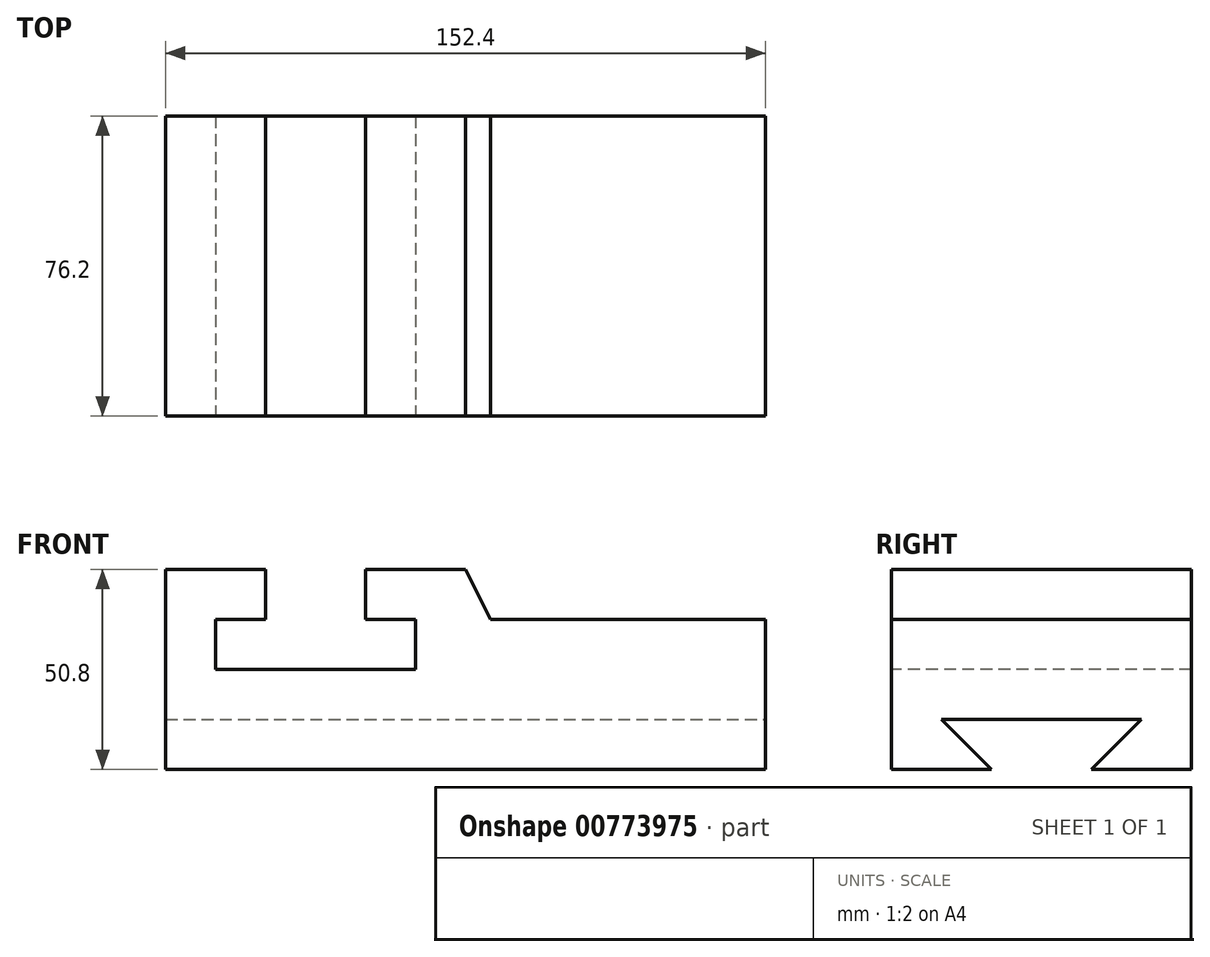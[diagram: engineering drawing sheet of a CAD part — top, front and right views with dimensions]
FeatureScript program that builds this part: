
annotation { "Feature Type Name" : "Feature", "Feature Type Description" : "" }
export const myFeature = defineFeature(function(context is Context, id is Id, definition is map)
    precondition{}
    {
        {
            var Q0;
            Q0=qCreatedBy(makeId("Front.planeOp"),FACE);
            var sketch = newSketch(context, id + "F0", { "sketchPlane" : qUnion([Q0])});
            skLineSegment(sketch, "E0", {"start": v(0, 0) * mm, "end": v(152.4, 0) * mm});
            skLineSegment(sketch, "E1", {"start": v(152.4, 0) * mm, "end": v(152.4, 50.8) * mm});
            skLineSegment(sketch, "E2", {"start": v(152.4, 50.8) * mm, "end": v(0, 50.8) * mm});
            skLineSegment(sketch, "E3", {"start": v(0, 50.8) * mm, "end": v(0, 0) * mm});
            skSolve(sketch);
        }
        {
            var Q0;
            Q0=makeQuery(id+"F0.imprint","IMPRINT",FACE,{"disambiguationData":[TD([[makeQuery(id+"F0.imprint","IMPRINT",EDGE,{"derivedFrom":sQuery(id+"F0.wireOp",EDGE,"E0")}),1.0]])]});
            extrude(context, id + "F1", {"entities" : qUnion([Q0]), "depth" : 76.2 * mm, "offsetDistance" : 25.4 * mm});
        }
        {
            var Q0;
            Q0=makeQuery(id+"F1.opExtrude","CAP_FACE",FACE,{"disambiguationData":[OSD([sQuery(id+"F0.wireOp",EDGE,"E0"),sQuery(id+"F0.wireOp",EDGE,"E1"),sQuery(id+"F0.wireOp",EDGE,"E2"),sQuery(id+"F0.wireOp",EDGE,"E3")])],"isStart":false});
            var sketch = newSketch(context, id + "F2", { "sketchPlane" : qUnion([Q0])});
            skLineSegment(sketch, "E4", {"start": v(152.4, 50.8) * mm, "end": v(152.4, 38.1) * mm});
            skLineSegment(sketch, "E5", {"start": v(152.4, 38.1) * mm, "end": v(82.55, 38.1) * mm});
            skLineSegment(sketch, "E6", {"start": v(82.55, 38.1) * mm, "end": v(82.55, 50.8) * mm});
            skLineSegment(sketch, "E7", {"start": v(82.55, 50.8) * mm, "end": v(152.4, 50.8) * mm});
            skSolve(sketch);
        }
        {
            var Q0;
            Q0=makeQuery(id+"F2.imprint","IMPRINT",FACE,{"disambiguationData":[TD([[makeQuery(id+"F2.imprint","IMPRINT",EDGE,{"derivedFrom":sQuery(id+"F2.wireOp",EDGE,"E4")}),1.0]])]});
            extrude(context, id + "F3", {"entities" : qUnion([Q0]), "operationType" : NewBodyOperationType.REMOVE, "oppositeDirection" : true, "depth" : 76.2 * mm, "offsetDistance" : 25.4 * mm});
        }
        {
            var Q0;
            Q0=makeQuery(id+"F1.opExtrude","CAP_FACE",FACE,{"disambiguationData":[OSD([sQuery(id+"F0.wireOp",EDGE,"E0"),sQuery(id+"F0.wireOp",EDGE,"E1"),sQuery(id+"F0.wireOp",EDGE,"E2"),sQuery(id+"F0.wireOp",EDGE,"E3")])],"isStart":false});
            var sketch = newSketch(context, id + "F4", { "sketchPlane" : qUnion([Q0])});
            skLineSegment(sketch, "E8", {"start": v(82.55, 38.1) * mm, "end": v(76.2, 38.1) * mm});
            skLineSegment(sketch, "E9", {"start": v(76.2, 38.1) * mm, "end": v(76.2, 50.8) * mm});
            skLineSegment(sketch, "E10", {"start": v(76.2, 50.8) * mm, "end": v(82.55, 38.1) * mm});
            skSolve(sketch);
        }
        {
            var Q0;
            {var subQ0=sQuery(id+"F4.wireOp",EDGE,"E10");Q0=makeQuery(id+"F4.imprint","IMPRINT",FACE,{"disambiguationData":[TD([[makeQuery(id+"F4.imprint","IMPRINT",EDGE,{"derivedFrom":subQ0}),1.0]])]});}
            extrude(context, id + "F5", {"entities" : qUnion([Q0]), "operationType" : NewBodyOperationType.REMOVE, "oppositeDirection" : true, "depth" : 76.2 * mm, "offsetDistance" : 25.4 * mm});
        }
        {
            var Q0;
            Q0=makeQuery(id+"F1.opExtrude","CAP_FACE",FACE,{"disambiguationData":[OSD([sQuery(id+"F0.wireOp",EDGE,"E0"),sQuery(id+"F0.wireOp",EDGE,"E1"),sQuery(id+"F0.wireOp",EDGE,"E2"),sQuery(id+"F0.wireOp",EDGE,"E3")])],"isStart":false});
            var sketch = newSketch(context, id + "F6", { "sketchPlane" : qUnion([Q0])});
            skLineSegment(sketch, "E11", {"start": v(50.8, 50.8) * mm, "end": v(50.8, 25.4) * mm});
            skLineSegment(sketch, "E12", {"start": v(50.8, 25.4) * mm, "end": v(25.4, 25.4) * mm});
            skLineSegment(sketch, "E13", {"start": v(25.4, 25.4) * mm, "end": v(25.4, 50.8) * mm});
            skLineSegment(sketch, "E14", {"start": v(25.4, 50.8) * mm, "end": v(50.8, 50.8) * mm});
            skSolve(sketch);
        }
        {
            var Q0;
            Q0=makeQuery(id+"F6.imprint","IMPRINT",FACE,{"disambiguationData":[TD([[makeQuery(id+"F6.imprint","IMPRINT",EDGE,{"derivedFrom":sQuery(id+"F6.wireOp",EDGE,"E11")}),-1.0]])]});
            extrude(context, id + "F7", {"entities" : qUnion([Q0]), "operationType" : NewBodyOperationType.REMOVE, "oppositeDirection" : true, "depth" : 76.2 * mm, "offsetDistance" : 25.4 * mm});
        }
        {
            var Q0;
            Q0=makeQuery(id+"F1.opExtrude","CAP_FACE",FACE,{"disambiguationData":[OSD([sQuery(id+"F0.wireOp",EDGE,"E0"),sQuery(id+"F0.wireOp",EDGE,"E1"),sQuery(id+"F0.wireOp",EDGE,"E2"),sQuery(id+"F0.wireOp",EDGE,"E3")])],"isStart":false});
            var sketch = newSketch(context, id + "F8", { "sketchPlane" : qUnion([Q0])});
            skLineSegment(sketch, "E15", {"start": v(25.4, 25.4) * mm, "end": v(12.7, 25.4) * mm});
            skLineSegment(sketch, "E16", {"start": v(12.7, 25.4) * mm, "end": v(12.7, 38.1) * mm});
            skLineSegment(sketch, "E17", {"start": v(12.7, 38.1) * mm, "end": v(25.4, 38.1) * mm});
            skLineSegment(sketch, "E18", {"start": v(25.4, 38.1) * mm, "end": v(25.4, 25.4) * mm});
            skSolve(sketch);
        }
        {
            var Q0;
            Q0=makeQuery(id+"F8.imprint","IMPRINT",FACE,{"disambiguationData":[TD([[makeQuery(id+"F8.imprint","IMPRINT",EDGE,{"derivedFrom":sQuery(id+"F8.wireOp",EDGE,"E15")}),-1.0]])]});
            extrude(context, id + "F9", {"entities" : qUnion([Q0]), "operationType" : NewBodyOperationType.REMOVE, "oppositeDirection" : true, "depth" : 76.2 * mm, "offsetDistance" : 25.4 * mm});
        }
        {
            var Q0;
            Q0=makeQuery(id+"F1.opExtrude","CAP_FACE",FACE,{"disambiguationData":[OSD([sQuery(id+"F0.wireOp",EDGE,"E0"),sQuery(id+"F0.wireOp",EDGE,"E1"),sQuery(id+"F0.wireOp",EDGE,"E2"),sQuery(id+"F0.wireOp",EDGE,"E3")])],"isStart":false});
            var sketch = newSketch(context, id + "F10", { "sketchPlane" : qUnion([Q0])});
            skLineSegment(sketch, "E19", {"start": v(50.8, 25.4) * mm, "end": v(63.5, 25.4) * mm});
            skLineSegment(sketch, "E20", {"start": v(63.5, 25.4) * mm, "end": v(63.5, 38.1) * mm});
            skLineSegment(sketch, "E21", {"start": v(63.5, 38.1) * mm, "end": v(50.8, 38.1) * mm});
            skLineSegment(sketch, "E22", {"start": v(50.8, 38.1) * mm, "end": v(50.8, 25.4) * mm});
            skSolve(sketch);
        }
        {
            var Q0;
            Q0=makeQuery(id+"F10.imprint","IMPRINT",FACE,{"disambiguationData":[TD([[makeQuery(id+"F10.imprint","IMPRINT",EDGE,{"derivedFrom":sQuery(id+"F10.wireOp",EDGE,"E19")}),1.0]])]});
            extrude(context, id + "F11", {"entities" : qUnion([Q0]), "operationType" : NewBodyOperationType.REMOVE, "oppositeDirection" : true, "depth" : 76.2 * mm, "offsetDistance" : 25.4 * mm});
        }
        {
            var Q0;
            Q0=makeQuery(id+"F1.opExtrude","SWEPT_FACE",FACE,{"disambiguationData":[OSD([sQuery(id+"F0.wireOp",EDGE,"E1")])]});
            var sketch = newSketch(context, id + "F12", { "sketchPlane" : qUnion([Q0])});
            skLineSegment(sketch, "E23", {"start": v(-25.4, 0) * mm, "end": v(-12.7, 12.7) * mm});
            skLineSegment(sketch, "E24", {"start": v(-12.7, 12.7) * mm, "end": v(-63.5, 12.7) * mm});
            skLineSegment(sketch, "E25", {"start": v(-50.8, 0) * mm, "end": v(-63.5, 12.7) * mm});
            skLineSegment(sketch, "E26", {"start": v(-50.8, 0) * mm, "end": v(-25.4, 0) * mm});
            skSolve(sketch);
        }
        {
            var Q0;
            Q0=makeQuery(id+"F12.imprint","IMPRINT",FACE,{"disambiguationData":[TD([[makeQuery(id+"F12.imprint","IMPRINT",EDGE,{"derivedFrom":sQuery(id+"F12.wireOp",EDGE,"E23")}),1.0]])]});
            extrude(context, id + "F13", {"entities" : qUnion([Q0]), "operationType" : NewBodyOperationType.REMOVE, "oppositeDirection" : true, "depth" : 152.4 * mm, "offsetDistance" : 25.4 * mm});
        }
    });
